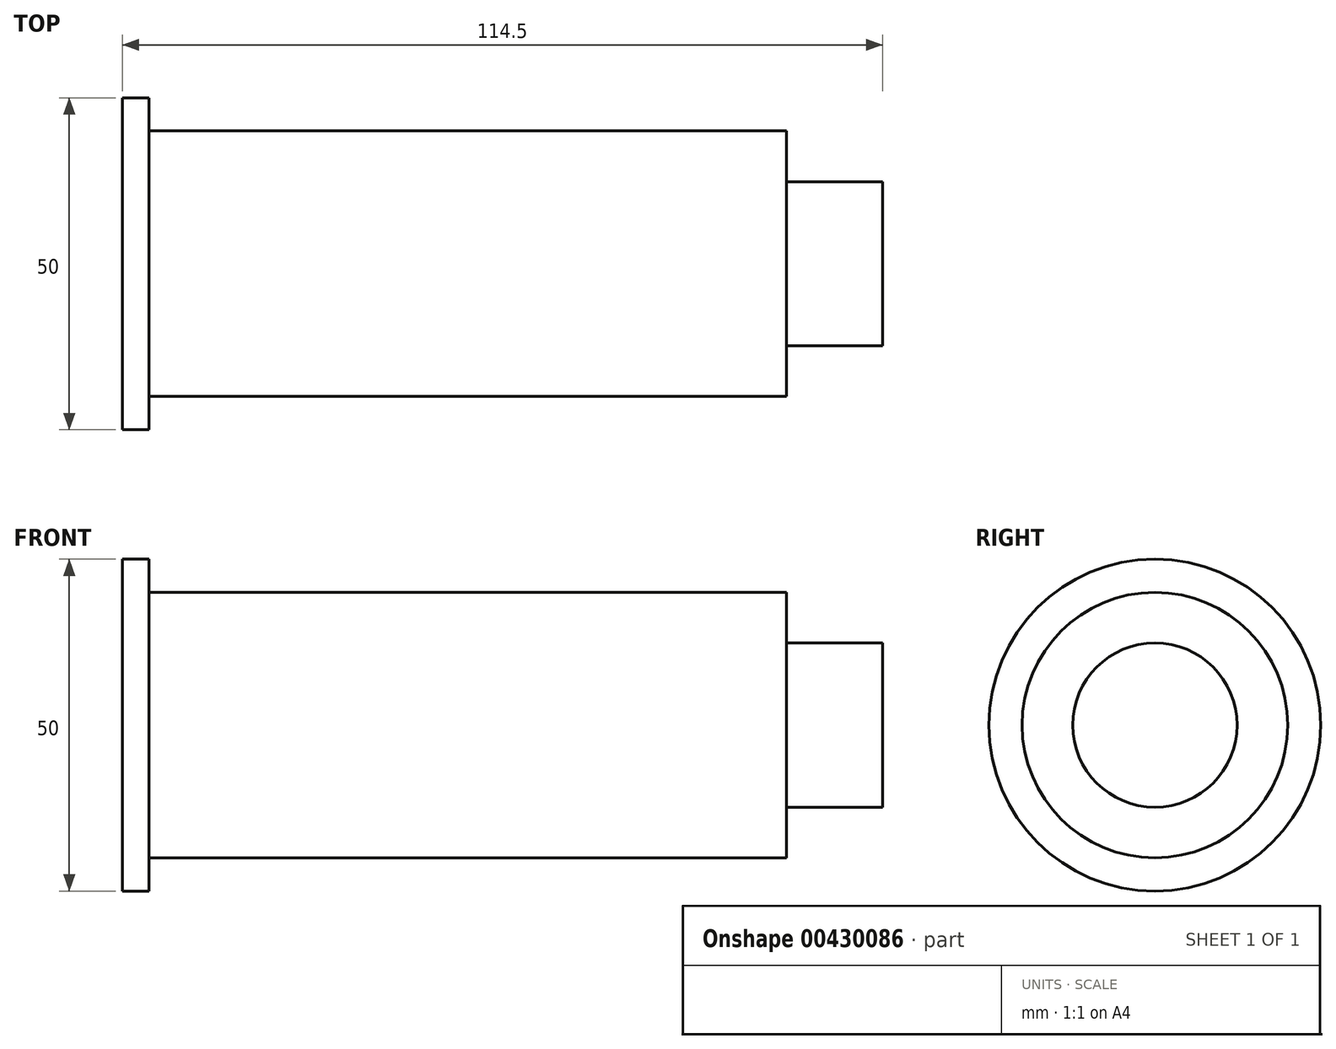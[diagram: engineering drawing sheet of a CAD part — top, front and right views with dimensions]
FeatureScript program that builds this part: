
annotation { "Feature Type Name" : "Feature", "Feature Type Description" : "" }
export const myFeature = defineFeature(function(context is Context, id is Id, definition is map)
    precondition{}
    {
        {
            var Q0;
            Q0=qCreatedBy(makeId("Front.planeOp"),FACE);
            var sketch = newSketch(context, id + "F0", { "sketchPlane" : qUnion([Q0])});
            skLineSegment(sketch, "E0.bottom", {"start": v(0, 0) * mm, "end": v(-100, 0) * mm});
            skLineSegment(sketch, "E0.top", {"start": v(0, 20) * mm, "end": v(-96, 20) * mm});
            skLineSegment(sketch, "E0.left", {"start": v(0, 0) * mm, "end": v(0, 20) * mm});
            skLineSegment(sketch, "E0.right", {"start": v(-100, 0) * mm, "end": v(-100, 20) * mm});
            skLineSegment(sketch, "E1.top", {"start": v(-100, 25) * mm, "end": v(-96, 25) * mm});
            skLineSegment(sketch, "E1.left", {"start": v(-100, 20) * mm, "end": v(-100, 25) * mm});
            skLineSegment(sketch, "E1.right", {"start": v(-96, 20) * mm, "end": v(-96, 25) * mm});
            skSolve(sketch);
        }
        {
            var Q0;
            Q0=makeQuery(id+"F0.imprint","IMPRINT",FACE,{"disambiguationData":[TD([[makeQuery(id+"F0.imprint","IMPRINT",EDGE,{"derivedFrom":sQuery(id+"F0.wireOp",EDGE,"E0.bottom")}),-1.0]])]});
            var Q1;
            Q1=sQuery(id+"F0.wireOp",EDGE,"E0.bottom");
            revolve(context, id + "F1", {"entities" : qUnion([Q0]), "axis" : qUnion([Q1]), "revolveType" : RevolveType.FULL});
        }
        {
            var Q0;
            Q0=makeQuery(id+"F1.opRevolve","SWEPT_FACE",FACE,{"disambiguationData":[OSD([sQuery(id+"F0.wireOp",EDGE,"E0.left")])]});
            var sketch = newSketch(context, id + "F2", { "sketchPlane" : qUnion([Q0])});
            skCircle(sketch, "E2", {"center": v(0, 0) * mm, "radius": 12.37 * mm});
            skSolve(sketch);
        }
        {
            var Q0;
            Q0 = qSketchRegion(id + "F2", true);
            extrude(context, id + "F3", {"entities" : qUnion([Q0]), "operationType" : NewBodyOperationType.ADD, "depth" : 14.5 * mm});
        }
    });
